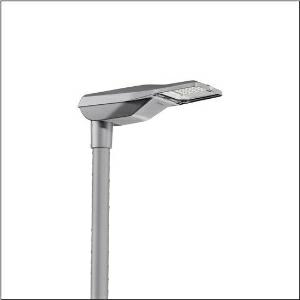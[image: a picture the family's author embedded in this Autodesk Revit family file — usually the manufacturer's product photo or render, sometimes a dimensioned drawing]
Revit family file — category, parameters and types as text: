
# Revit family: streetlight_sl_21_iq_micro___p0_5a_5xe1v31g08db_d973
name_source: partatom
category: Lighting Fixtures
units: mm (PartAtom-declared; Revit-internal decimal feet)

## family parameters
Cut with Voids When Loaded = No
Host = Face
Light Source = No
Part Type = Normal
Room Calculation Point = No
Round Connector Dimension = Use Diameter
Shared = No

## types (1)
- --- (1 x LED, 4660 lm, 36.4 W, 3000K)
    Apparent Load = 36 VA
    CIE Flux Codes = 37 73 96 100 100
    Color Rendering = 70
    Color Temperature = 3000K
    Default Elevation = 1800 mm
    Description = Streetlight SL 21 iQ micro, mast luminaire, primary light control with lens, of PMMA, primary optical cover: cover, of toughened safety glass, transparent, light distribution: P0.5a, light emission: direct distribution, primary light characteristic: asymmetric, installation type: post-top, side-entry, LED, High Power LED, rated luminous flux: 4.660lm, luminous efficacy: 128lm/W, light colour: 730, colour temperature: 3000K, control gear: iQ Street-Remote, control: pre-setting: linear dimming characteristic, Street-Remote, Auto-Match, Temp-Guard, Lumen-Switch, Night-Set, Smart-Wire, Light-Fading, Desk-Remote (wireless, voltage-free reading and setting of iQ features in the workshop via application-optimized NFC function/RFID function), optimised constant luminous flux control (CLO 2.0), mains connection: 220..240V, AC, 50/60Hz, start of lifetime: 36W, end of service life: 38W, reduction: 16W, luminaire housing, of diecast aluminium, powder-coated, Siteco® metallic grey (DB 702S), corrosivity category C5 mid according to DIN EN ISO 12944, please order mast flange separately, inclination adjustable: 0°, 5°, 10°, 15°, sealing non-destructively replaceable, multi-level sealing system, length: 528mm, width: 235mm, height: 110mm, mast flange for spigot size: 42mm (side-entry): 5XC10008XM4, 60/48mm (side-entry/post-top): 5XC10108XM2, 76/60mm (side-entry/post-top): 5XC10108XM1, protection rating (complete): IP66, insulation class (complete): insulation class II (safety insulation), certification: CE, ENEC, ENEC+, VDE, impact resistance: IK10, permissible operating ambient temperature for outdoor applications: -40..+50°C, standard-compliant lighting for roads and squares, packaging unit: 1 piece

Light Distribution: P0.5a
    Height = 110 mm
    Lamp = 1 x LED
    Lamp Light Flux = 4660 lm
    Lamp Power = 36.4 W
    Lamp count = 1
    Length = 528 mm
    Luminous efficacy = 128 lm/W
    Manufacturer = Siteco
    ModVariant = No
    Model = 5XE1V31G08DB
    Number of Poles = 1
    OnlyDefault = Yes
    Power Factor = 1
    Product Name = Streetlight SL 21 iQ micro | P0.5a
    Product group = mast luminaire | pylon top
    ProductGroupID = 6100
    Protection Class = Protection class II
    Protection Degree = IP 66
    RLX_Detail_Level = 1
    RLX_Emergency_Light_Flux = 0 lm
    RLX_Emergency_Type = 0
    RLX_Emergency_Type_DB = No
    RlxData = <blob elided: 98309 chars, md5=ac1932de>
    Socket = socket
    Standby Power = 0 W
    System Light Flux = 4660 lm
    System Power = 36 W
    Type Comments = factory setting: luminous flux: 100 % | dim-lin: 254 | 715 mA
    Type Image = l_1006881.jpg
    URL = http://relux.com
    VarID = @adj_091889
    Voltage = 0 V
    Weight = 0.00 kg
    Width = 235 mm

## geometry (parser evidence)
native form markers: Blend x4, Sweep x12
no freeform markers — native parametric forms only
